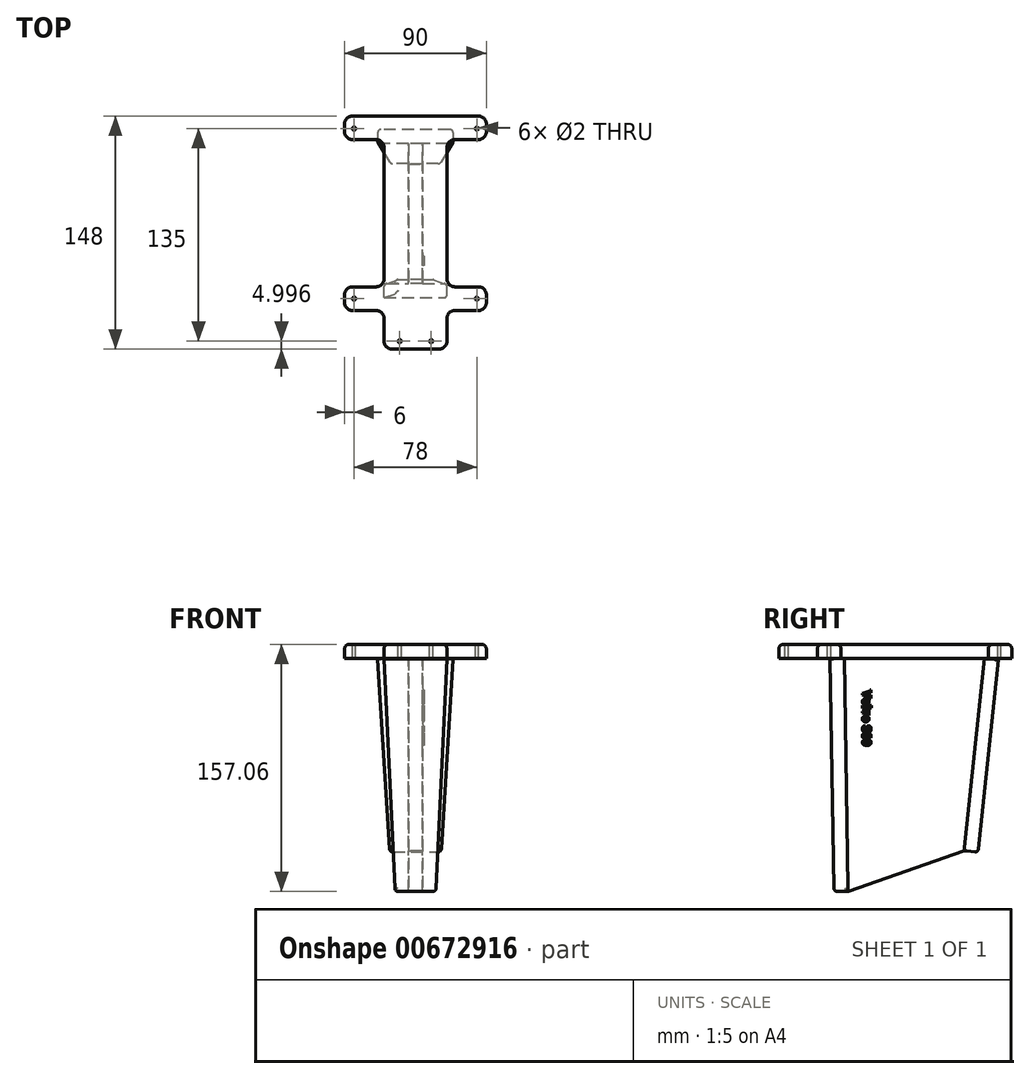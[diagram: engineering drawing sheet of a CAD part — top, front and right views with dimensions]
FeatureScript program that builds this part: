
annotation { "Feature Type Name" : "Feature", "Feature Type Description" : "" }
export const myFeature = defineFeature(function(context is Context, id is Id, definition is map)
    precondition{}
    {
        {
            var Q0;
            Q0=qCreatedBy(makeId("Top.planeOp"),FACE);
            var sketch = newSketch(context, id + "F0", { "sketchPlane" : qUnion([Q0])});
            skLineSegment(sketch, "E0", {"start": v(0, 69.42) * mm, "end": v(-40, 69.42) * mm});
            skLineSegment(sketch, "E1", {"start": v(-15, -78.58) * mm, "end": v(0, -78.58) * mm});
            skLineSegment(sketch, "E2", {"start": v(-45, 59.42) * mm, "end": v(-45, 64.42) * mm});
            skCircle(sketch, "E3", {"center": v(-39, 61.42) * mm, "radius": 1 * mm});
            skCircle(sketch, "E4", {"center": v(-39, -46.58) * mm, "radius": 1 * mm});
            skCircle(sketch, "E5.MirrorC", {"center": v(39, 61.42) * mm, "radius": 1 * mm});
            skCircle(sketch, "E6.MirrorC", {"center": v(39, -46.58) * mm, "radius": 1 * mm});
            skCircle(sketch, "E7", {"center": v(-10, -73.58) * mm, "radius": 1 * mm});
            skCircle(sketch, "E8.MirrorC", {"center": v(10, -73.58) * mm, "radius": 1 * mm});
            skLineSegment(sketch, "E9", {"start": v(-39, -46.58) * mm, "end": v(-10, -73.58) * mm, "construction": true});
            skLineSegment(sketch, "E10", {"start": v(-40, -54.08) * mm, "end": v(-25, -54.08) * mm});
            skLineSegment(sketch, "E11", {"start": v(-20, -59.08) * mm, "end": v(-20, -73.58) * mm});
            skLineSegment(sketch, "E12.MirrorCS", {"start": v(15, -78.58) * mm, "end": v(0, -78.58) * mm});
            skLineSegment(sketch, "E13.MirrorCS", {"start": v(20, -59.08) * mm, "end": v(20, -73.58) * mm});
            skLineSegment(sketch, "E14.MirrorCS", {"start": v(40, -54.08) * mm, "end": v(25, -54.08) * mm});
            skLineSegment(sketch, "E15", {"start": v(-45, -49.08) * mm, "end": v(-45, -44.08) * mm});
            skLineSegment(sketch, "E16", {"start": v(-40, -39.08) * mm, "end": v(-25, -39.08) * mm});
            skLineSegment(sketch, "E17", {"start": v(-20, -34.08) * mm, "end": v(-20, 49.42) * mm});
            skLineSegment(sketch, "E18", {"start": v(-25, 54.42) * mm, "end": v(-40, 54.42) * mm});
            skLineSegment(sketch, "E19.MirrorCS", {"start": v(0, 69.42) * mm, "end": v(40, 69.42) * mm});
            skLineSegment(sketch, "E20.MirrorCS", {"start": v(45, 59.42) * mm, "end": v(45, 64.42) * mm});
            skLineSegment(sketch, "E21.MirrorCS", {"start": v(25, 54.42) * mm, "end": v(40, 54.42) * mm});
            skLineSegment(sketch, "E22.MirrorCS", {"start": v(20, -34.08) * mm, "end": v(20, 49.42) * mm});
            skLineSegment(sketch, "E23.MirrorCS", {"start": v(45, -49.08) * mm, "end": v(45, -44.08) * mm});
            skLineSegment(sketch, "E24.MirrorCS", {"start": v(40, -39.08) * mm, "end": v(25, -39.08) * mm});
            skPoint(sketch, "E25.visualSharp", {"position": v(-45, 69.42) * mm});
            skArc(sketch, "E25.filletArc", {"start": v(-40, 69.42) * mm, "mid": v(-43.54, 67.95) * mm, "end": v(-45, 64.42) * mm});
            skPoint(sketch, "E26.visualSharp", {"position": v(-45, 54.42) * mm});
            skArc(sketch, "E26.filletArc", {"start": v(-45, 59.42) * mm, "mid": v(-43.54, 55.88) * mm, "end": v(-40, 54.42) * mm});
            skPoint(sketch, "E27.visualSharp", {"position": v(-20, 54.42) * mm});
            skArc(sketch, "E27.filletArc", {"start": v(-20, 49.42) * mm, "mid": v(-21.46, 52.95) * mm, "end": v(-25, 54.42) * mm});
            skPoint(sketch, "E28.visualSharp", {"position": v(-20, -39.08) * mm});
            skArc(sketch, "E28.filletArc", {"start": v(-25, -39.08) * mm, "mid": v(-21.46, -37.62) * mm, "end": v(-20, -34.08) * mm});
            skPoint(sketch, "E29.visualSharp", {"position": v(-45, -39.08) * mm});
            skArc(sketch, "E29.filletArc", {"start": v(-40, -39.08) * mm, "mid": v(-43.54, -40.55) * mm, "end": v(-45, -44.08) * mm});
            skPoint(sketch, "E30.visualSharp", {"position": v(-45, -54.08) * mm});
            skArc(sketch, "E30.filletArc", {"start": v(-45, -49.08) * mm, "mid": v(-43.54, -52.62) * mm, "end": v(-40, -54.08) * mm});
            skPoint(sketch, "E31.visualSharp", {"position": v(-20, -54.08) * mm});
            skArc(sketch, "E31.filletArc", {"start": v(-20, -59.08) * mm, "mid": v(-21.46, -55.55) * mm, "end": v(-25, -54.08) * mm});
            skPoint(sketch, "E32.visualSharp", {"position": v(-20, -78.58) * mm});
            skArc(sketch, "E32.filletArc", {"start": v(-20, -73.58) * mm, "mid": v(-18.54, -77.12) * mm, "end": v(-15, -78.58) * mm});
            skPoint(sketch, "E33.visualSharp", {"position": v(45, 69.42) * mm});
            skArc(sketch, "E33.filletArc", {"start": v(45, 64.42) * mm, "mid": v(43.54, 67.95) * mm, "end": v(40, 69.42) * mm});
            skPoint(sketch, "E34.visualSharp", {"position": v(45, 54.42) * mm});
            skArc(sketch, "E34.filletArc", {"start": v(40, 54.42) * mm, "mid": v(43.54, 55.88) * mm, "end": v(45, 59.42) * mm});
            skPoint(sketch, "E35.visualSharp", {"position": v(20, 54.42) * mm});
            skArc(sketch, "E35.filletArc", {"start": v(25, 54.42) * mm, "mid": v(21.46, 52.95) * mm, "end": v(20, 49.42) * mm});
            skPoint(sketch, "E36.visualSharp", {"position": v(20, -39.08) * mm});
            skArc(sketch, "E36.filletArc", {"start": v(20, -34.08) * mm, "mid": v(21.46, -37.62) * mm, "end": v(25, -39.08) * mm});
            skPoint(sketch, "E37.visualSharp", {"position": v(45, -39.08) * mm});
            skArc(sketch, "E37.filletArc", {"start": v(45, -44.08) * mm, "mid": v(43.54, -40.55) * mm, "end": v(40, -39.08) * mm});
            skPoint(sketch, "E38.visualSharp", {"position": v(45, -54.08) * mm});
            skArc(sketch, "E38.filletArc", {"start": v(40, -54.08) * mm, "mid": v(43.54, -52.62) * mm, "end": v(45, -49.08) * mm});
            skPoint(sketch, "E39.visualSharp", {"position": v(20, -54.08) * mm});
            skArc(sketch, "E39.filletArc", {"start": v(25, -54.08) * mm, "mid": v(21.46, -55.55) * mm, "end": v(20, -59.08) * mm});
            skPoint(sketch, "E40.visualSharp", {"position": v(20, -78.58) * mm});
            skArc(sketch, "E40.filletArc", {"start": v(15, -78.58) * mm, "mid": v(18.54, -77.12) * mm, "end": v(20, -73.58) * mm});
            skSolve(sketch);
        }
        {
            var Q0;
            Q0 = qSketchRegion(id + "F0", true);
            extrude(context, id + "F1", {"entities" : qUnion([Q0]), "oppositeDirection" : true, "depth" : 9 * mm, "offsetDistance" : 25 * mm});
        }
        {
            var Q0;
            Q0=makeQuery(id+"F1.opExtrude","CAP_EDGE",EDGE,{"disambiguationData":[OSD([sQuery(id+"F0.wireOp",EDGE,"E25.filletArc")])],"isStart":true});
            fillet(context, id + "F2", {"entities" : qUnion([Q0]), "radius" : 3 * mm, "tangentPropagation" : true, "allowEdgeOverflow" : false});
        }
        {
            var Q0;
            Q0=qCreatedBy(makeId("Right.planeOp"),FACE);
            var sketch = newSketch(context, id + "F3", { "sketchPlane" : qUnion([Q0])});
            skLineSegment(sketch, "E41", {"start": v(51.83, -9.08) * mm, "end": v(-37.03, -9.08) * mm});
            skLineSegment(sketch, "E42", {"start": v(-37.03, -9.08) * mm, "end": v(-34.52, -157.06) * mm});
            skLineSegment(sketch, "E43", {"start": v(-34.52, -157.06) * mm, "end": v(38.94, -131.4) * mm});
            skLineSegment(sketch, "E44", {"start": v(38.94, -131.4) * mm, "end": v(51.83, -9.08) * mm});
            skSolve(sketch);
        }
        {
            var Q0;
            Q0 = qSketchRegion(id + "F3", true);
            extrude(context, id + "F4", {"entities" : qUnion([Q0]), "endBound" : BoundingType.SYMMETRIC, "depth" : 9 * mm, "offsetDistance" : 25 * mm});
        }
        {
            var Q0;
            Q0=makeQuery(id+"F4.opExtrude","SWEPT_FACE",FACE,{"disambiguationData":[OSD([sQuery(id+"F3.wireOp",EDGE,"E44")])]});
            var sketch = newSketch(context, id + "F5", { "sketchPlane" : qUnion([Q0])});
            skLineSegment(sketch, "E45", {"start": v(0, -3.6) * mm, "end": v(24, -3.6) * mm});
            skLineSegment(sketch, "E46", {"start": v(24, -3.6) * mm, "end": v(16.33, -126.36) * mm});
            skLineSegment(sketch, "E47", {"start": v(16.33, -126.36) * mm, "end": v(0, -126.36) * mm});
            skLineSegment(sketch, "E48.MirrorCS", {"start": v(0, -3.6) * mm, "end": v(-24, -3.6) * mm});
            skLineSegment(sketch, "E49.MirrorCS", {"start": v(-24, -3.6) * mm, "end": v(-16.33, -126.36) * mm});
            skLineSegment(sketch, "E50.MirrorCS", {"start": v(-16.33, -126.36) * mm, "end": v(0, -126.36) * mm});
            skSolve(sketch);
        }
        {
            var Q0;
            Q0 = qSketchRegion(id + "F5", true);
            extrude(context, id + "F6", {"entities" : qUnion([Q0]), "operationType" : NewBodyOperationType.ADD, "depth" : 9 * mm, "offsetDistance" : 25 * mm});
        }
        {
            var Q0;
            Q0=makeQuery(id+"F4.opExtrude","SWEPT_FACE",FACE,{"disambiguationData":[OSD([sQuery(id+"F3.wireOp",EDGE,"E42")])]});
            var sketch = newSketch(context, id + "F7", { "sketchPlane" : qUnion([Q0])});
            skLineSegment(sketch, "E51", {"start": v(0, -8.45) * mm, "end": v(20, -8.45) * mm});
            skLineSegment(sketch, "E52", {"start": v(20, -8.45) * mm, "end": v(13, -156.29) * mm});
            skLineSegment(sketch, "E53", {"start": v(13, -156.29) * mm, "end": v(0, -156.29) * mm});
            skLineSegment(sketch, "E54.MirrorCS", {"start": v(0, -8.45) * mm, "end": v(-20, -8.45) * mm});
            skLineSegment(sketch, "E55.MirrorCS", {"start": v(-20, -8.45) * mm, "end": v(-13, -156.29) * mm});
            skLineSegment(sketch, "E56.MirrorCS", {"start": v(-13, -156.29) * mm, "end": v(0, -156.29) * mm});
            skSolve(sketch);
        }
        {
            var Q0;
            Q0 = qSketchRegion(id + "F7", true);
            extrude(context, id + "F8", {"entities" : qUnion([Q0]), "operationType" : NewBodyOperationType.ADD, "depth" : 9 * mm, "offsetDistance" : 25 * mm});
        }
        {
            var Q0;
            Q0=makeQuery(id+"F4.opExtrude","CAP_FACE",FACE,{"disambiguationData":[OSD([sQuery(id+"F3.wireOp",EDGE,"E41"),sQuery(id+"F3.wireOp",EDGE,"E42"),sQuery(id+"F3.wireOp",EDGE,"E43"),sQuery(id+"F3.wireOp",EDGE,"E44")])],"isStart":false});
            var sketch = newSketch(context, id + "F9", { "sketchPlane" : qUnion([Q0])});
            skText(sketch, "E57", { "text": "Volvo S60", "fontName": "RobotoSlab-Bold.ttf"});
            const initialGuessF9  = {"E57": [-0.02543, -0.029, 0, -1, 0.00543]};
            skSetInitialGuess(sketch, initialGuessF9);
            skSolve(sketch);
        }
        {
            var Q0;
            Q0 = qSketchRegion(id + "F9", true);
            extrude(context, id + "F10", {"entities" : qUnion([Q0]), "operationType" : NewBodyOperationType.ADD, "depth" : 1 * mm, "offsetDistance" : 25 * mm});
        }
        {
            var Q0;
            Q0=makeQuery(id+"F6.opExtrude","CAP_EDGE",EDGE,{"disambiguationData":[OSD([sQuery(id+"F5.wireOp",EDGE,"E49.MirrorCS")])],"isStart":false});
            var Q1;
            Q1=makeQuery(id+"F8.opExtrude","CAP_EDGE",EDGE,{"disambiguationData":[OSD([sQuery(id+"F7.wireOp",EDGE,"E52")])],"isStart":false});
            var Q2;
            Q2=makeQuery(id+"F6.opExtrude","CAP_EDGE",EDGE,{"disambiguationData":[OSD([sQuery(id+"F5.wireOp",EDGE,"E47"),sQuery(id+"F5.wireOp",EDGE,"E50.MirrorCS")])],"isStart":false});
            var Q3;
            Q3=makeQuery(id+"F8.opExtrude","CAP_EDGE",EDGE,{"disambiguationData":[OSD([sQuery(id+"F7.wireOp",EDGE,"E53"),sQuery(id+"F7.wireOp",EDGE,"E56.MirrorCS")])],"isStart":false});
            var Q4;
            Q4=makeQuery(id+"F6.opExtrude","SWEPT_EDGE",EDGE,{"disambiguationData":[OSD([sQuery(id+"F5.wireOp",EDGE,"E49.MirrorCS"),sQuery(id+"F5.wireOp",EDGE,"E50.MirrorCS")])]});
            var Q5;
            Q5=makeQuery(id+"F6.opExtrude","SWEPT_EDGE",EDGE,{"disambiguationData":[OSD([sQuery(id+"F5.wireOp",EDGE,"E46"),sQuery(id+"F5.wireOp",EDGE,"E47")])]});
            var Q6;
            Q6=makeQuery(id+"F6.opExtrude","CAP_EDGE",EDGE,{"disambiguationData":[OSD([sQuery(id+"F5.wireOp",EDGE,"E46")])],"isStart":false});
            var Q7;
            Q7=makeQuery(id+"F8.opExtrude","CAP_EDGE",EDGE,{"disambiguationData":[OSD([sQuery(id+"F7.wireOp",EDGE,"E55.MirrorCS")])],"isStart":true});
            var Q8;
            Q8=makeQuery(id+"F8.opExtrude","SWEPT_EDGE",EDGE,{"disambiguationData":[OSD([sQuery(id+"F7.wireOp",EDGE,"E55.MirrorCS"),sQuery(id+"F7.wireOp",EDGE,"E56.MirrorCS")])]});
            var Q9;
            Q9=makeQuery(id+"F8.opExtrude","SWEPT_EDGE",EDGE,{"disambiguationData":[OSD([sQuery(id+"F7.wireOp",EDGE,"E52"),sQuery(id+"F7.wireOp",EDGE,"E53")])]});
            fillet(context, id + "F11", {"entities" : qUnion([Q0, Q1, Q2, Q3, Q4, Q5, Q6, Q7, Q8, Q9]), "radius" : 2 * mm, "tangentPropagation" : true, "allowEdgeOverflow" : false});
        }
        {
            var Q0;
            Q0=makeQuery(id+"F6.opExtrude","CAP_EDGE",EDGE,{"disambiguationData":[OSD([sQuery(id+"F5.wireOp",EDGE,"E49.MirrorCS")])],"isStart":true});
            var Q1;
            Q1=makeQuery(id+"F8.opExtrude","CAP_EDGE",EDGE,{"disambiguationData":[OSD([sQuery(id+"F7.wireOp",EDGE,"E52")])],"isStart":true});
            fillet(context, id + "F12", {"entities" : qUnion([Q0, Q1]), "radius" : 2 * mm, "tangentPropagation" : true, "allowEdgeOverflow" : false});
        }
        {
            var Q0;
            {var subQ0=sQuery(id+"F7.wireOp",EDGE,"E56.MirrorCS");var subQ1=sQuery(id+"F7.wireOp",EDGE,"E55.MirrorCS");var subQ2=sQuery(id+"F7.wireOp",EDGE,"E53");var subQ3=makeQuery(id+"F8.opExtrude","CAP_FACE",FACE,{"disambiguationData":[OSD([sQuery(id+"F7.wireOp",EDGE,"E51"),sQuery(id+"F7.wireOp",EDGE,"E52"),subQ2,sQuery(id+"F7.wireOp",EDGE,"E54.MirrorCS"),subQ1,subQ0])],"isStart":true});var subQ5=makeQuery(id+"F8.opExtrude","SWEPT_FACE",FACE,{"disambiguationData":[OSD([subQ2,subQ0])]});Q0=makeQuery(id+"F8.boolean.opBoolean","SPLIT",EDGE,{"disambiguationData":[topologyDisambiguationEdgeConnected([subQ3,subQ5]),TD([makeQuery(id+"F8.opExtrude","SWEPT_FACE",FACE,{"disambiguationData":[OSD([subQ1])]})])],"derivedFrom":makeQuery(id+"F8.opExtrude","CAP_EDGE",EDGE,{"disambiguationData":[OSD([subQ2,subQ0])],"isStart":true})});}
            var Q1;
            {var subQ0=sQuery(id+"F5.wireOp",EDGE,"E50.MirrorCS");var subQ1=sQuery(id+"F5.wireOp",EDGE,"E47");var subQ2=sQuery(id+"F5.wireOp",EDGE,"E46");var subQ3=makeQuery(id+"F6.opExtrude","CAP_FACE",FACE,{"disambiguationData":[OSD([sQuery(id+"F5.wireOp",EDGE,"E45"),subQ2,subQ1,sQuery(id+"F5.wireOp",EDGE,"E48.MirrorCS"),sQuery(id+"F5.wireOp",EDGE,"E49.MirrorCS"),subQ0])],"isStart":true});var subQ5=makeQuery(id+"F6.opExtrude","SWEPT_FACE",FACE,{"disambiguationData":[OSD([subQ1,subQ0])]});Q1=makeQuery(id+"F6.boolean.opBoolean","SPLIT",EDGE,{"disambiguationData":[topologyDisambiguationEdgeConnected([subQ3,subQ5]),TD([makeQuery(id+"F6.opExtrude","SWEPT_FACE",FACE,{"disambiguationData":[OSD([subQ2])]})])],"derivedFrom":makeQuery(id+"F6.opExtrude","CAP_EDGE",EDGE,{"disambiguationData":[OSD([subQ1,subQ0])],"isStart":true})});}
            fillet(context, id + "F13", {"entities" : qUnion([Q0, Q1]), "radius" : 2 * mm, "tangentPropagation" : true, "allowEdgeOverflow" : false});
        }
    });
